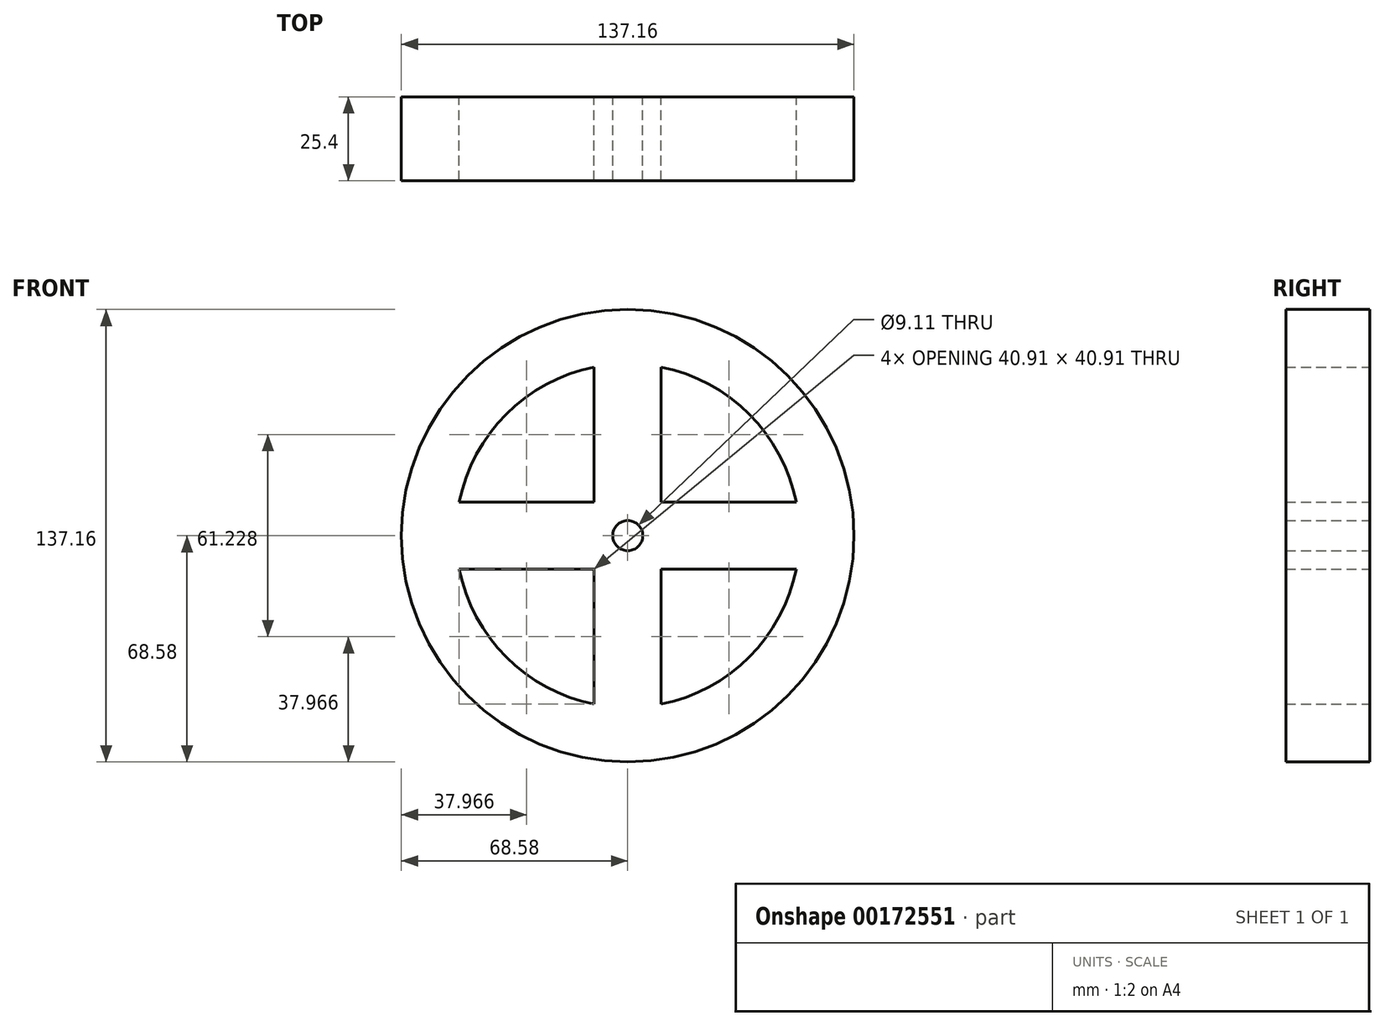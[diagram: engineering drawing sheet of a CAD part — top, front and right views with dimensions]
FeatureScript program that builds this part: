
annotation { "Feature Type Name" : "Feature", "Feature Type Description" : "" }
export const myFeature = defineFeature(function(context is Context, id is Id, definition is map)
    precondition{}
    {
        {
            var Q0;
            Q0=qCreatedBy(makeId("Front.planeOp"),FACE);
            var sketch = newSketch(context, id + "F0", { "sketchPlane" : qUnion([Q0])});
            skCircle(sketch, "E0", {"center": v(0, 0) * mm, "radius": 68.58 * mm});
            skArc(sketch, "E1", {"start": v(-51.07, -10.16) * mm, "mid": v(-36.82, -36.82) * mm, "end": v(-10.16, -51.07) * mm});
            skCircle(sketch, "E2", {"center": v(0, 0) * mm, "radius": 4.55 * mm});
            skLineSegment(sketch, "E3", {"start": v(0, 0) * mm, "end": v(52.07, 0) * mm});
            skLineSegment(sketch, "E4", {"start": v(0, 0) * mm, "end": v(0, 52.07) * mm});
            skLineSegment(sketch, "E5", {"start": v(0, 0) * mm, "end": v(-52.07, 0) * mm});
            skLineSegment(sketch, "E6", {"start": v(0, 0) * mm, "end": v(0, -52.07) * mm});
            skLineSegment(sketch, "E7.0", {"start": v(10.16, 10.16) * mm, "end": v(10.16, 51.07) * mm});
            skLineSegment(sketch, "E8.0", {"start": v(-10.16, 10.16) * mm, "end": v(-51.07, 10.16) * mm});
            skLineSegment(sketch, "E9.0", {"start": v(-10.16, -10.16) * mm, "end": v(-51.07, -10.16) * mm});
            skLineSegment(sketch, "E10.0", {"start": v(10.16, -10.16) * mm, "end": v(10.16, -51.07) * mm});
            skLineSegment(sketch, "E11.0", {"start": v(10.16, 10.16) * mm, "end": v(51.07, 10.16) * mm});
            skLineSegment(sketch, "E12.0", {"start": v(10.16, -10.16) * mm, "end": v(51.07, -10.16) * mm});
            skLineSegment(sketch, "E13.0", {"start": v(-10.16, 10.16) * mm, "end": v(-10.16, 51.07) * mm});
            skArc(sketch, "E14.trimOffspring", {"start": v(10.16, -51.07) * mm, "mid": v(36.82, -36.82) * mm, "end": v(51.07, -10.16) * mm});
            skArc(sketch, "E15.trimOffspring", {"start": v(51.07, 10.16) * mm, "mid": v(36.82, 36.82) * mm, "end": v(10.16, 51.07) * mm});
            skArc(sketch, "E16.trimOffspring", {"start": v(-10.16, 51.07) * mm, "mid": v(-36.82, 36.82) * mm, "end": v(-51.07, 10.16) * mm});
            skLineSegment(sketch, "E17.trimOffspring", {"start": v(-10.16, -15.86) * mm, "end": v(-10.16, -51.07) * mm});
            skLineSegment(sketch, "E18", {"start": v(-10.16, -15.86) * mm, "end": v(-10.16, -10.16) * mm});
            skSolve(sketch);
        }
        {
            var Q0;
            Q0=makeQuery(id+"F0.imprint","IMPRINT",FACE,{"disambiguationData":[TD([[makeQuery(id+"F0.imprint","IMPRINT",EDGE,{"derivedFrom":sQuery(id+"F0.wireOp",EDGE,"E0")}),1.0]])]});
            extrude(context, id + "F1", {"entities" : qUnion([Q0]), "endBound" : BoundingType.SYMMETRIC, "depth" : 25.4 * mm});
        }
    });
